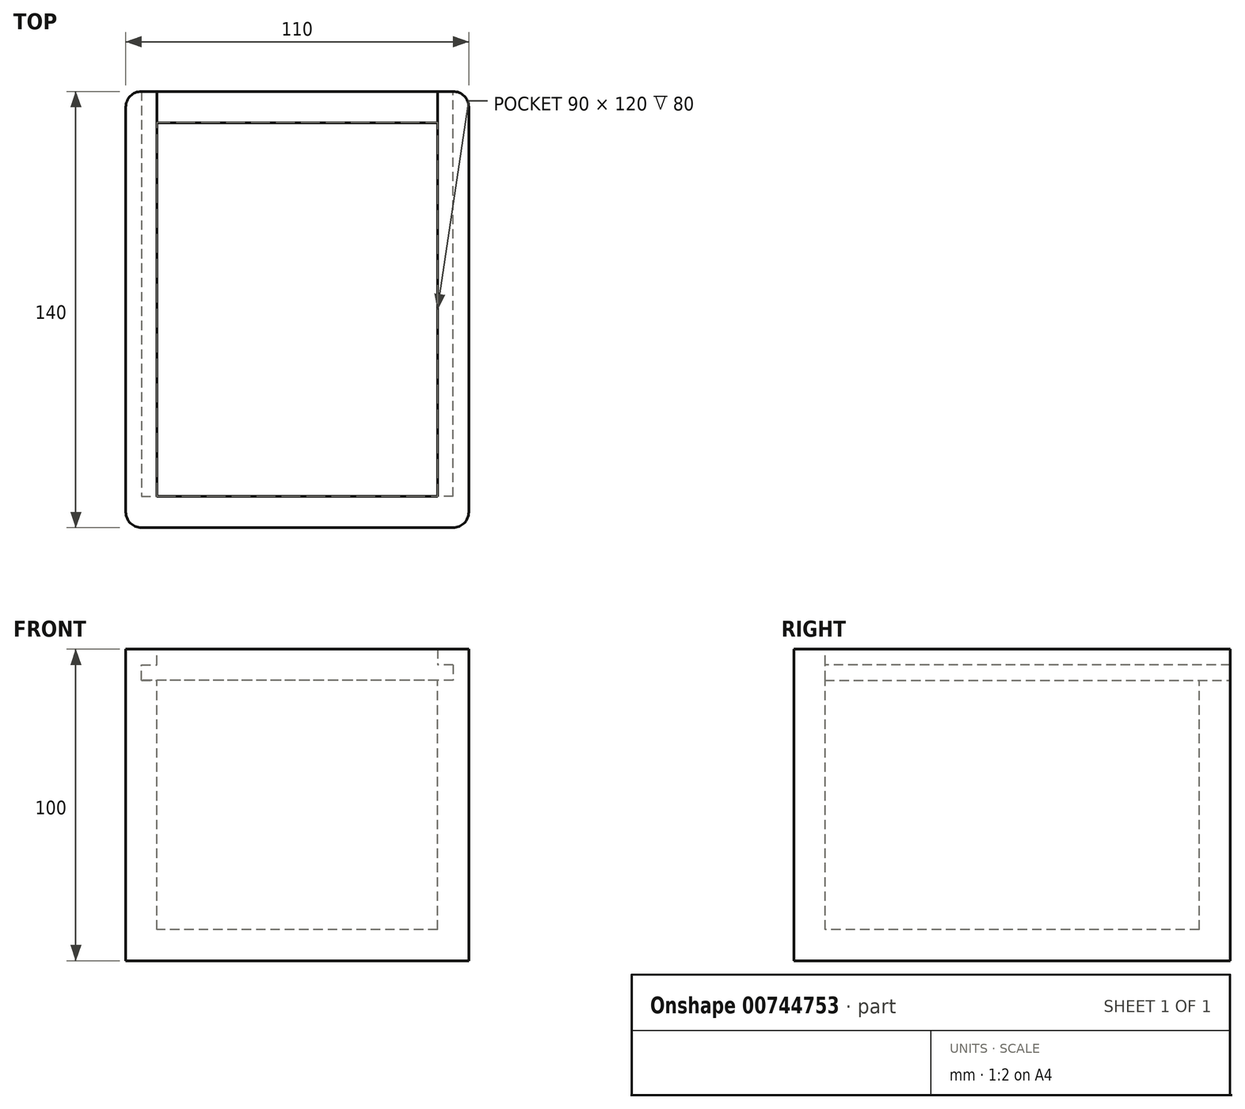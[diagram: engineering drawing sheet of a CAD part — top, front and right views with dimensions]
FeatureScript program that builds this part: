
annotation { "Feature Type Name" : "Feature", "Feature Type Description" : "" }
export const myFeature = defineFeature(function(context is Context, id is Id, definition is map)
    precondition{}
    {
        {
            var Q0;
            Q0=qCreatedBy(makeId("Top.planeOp"),FACE);
            var sketch = newSketch(context, id + "F0", { "sketchPlane" : qUnion([Q0])});
            skLineSegment(sketch, "E0.bottom", {"start": v(50, -70) * mm, "end": v(-50, -70) * mm});
            skLineSegment(sketch, "E0.top", {"start": v(50, 70) * mm, "end": v(-50, 70) * mm});
            skLineSegment(sketch, "E0.left", {"start": v(55, -65) * mm, "end": v(55, 65) * mm});
            skLineSegment(sketch, "E0.right", {"start": v(-55, -65) * mm, "end": v(-55, 65) * mm});
            skPoint(sketch, "E0.middle", {"position": v(0, 0) * mm});
            skPoint(sketch, "E1.visualSharp", {"position": v(-55, 70) * mm});
            skArc(sketch, "E1.filletArc", {"start": v(-50, 70) * mm, "mid": v(-53.54, 68.54) * mm, "end": v(-55, 65) * mm});
            skPoint(sketch, "E2.visualSharp", {"position": v(-55, -70) * mm});
            skArc(sketch, "E2.filletArc", {"start": v(-55, -65) * mm, "mid": v(-53.54, -68.54) * mm, "end": v(-50, -70) * mm});
            skPoint(sketch, "E3.visualSharp", {"position": v(55, -70) * mm});
            skArc(sketch, "E3.filletArc", {"start": v(50, -70) * mm, "mid": v(53.54, -68.54) * mm, "end": v(55, -65) * mm});
            skPoint(sketch, "E4.visualSharp", {"position": v(55, 70) * mm});
            skArc(sketch, "E4.filletArc", {"start": v(55, 65) * mm, "mid": v(53.54, 68.54) * mm, "end": v(50, 70) * mm});
            skSolve(sketch);
        }
        {
            var Q0;
            Q0=makeQuery(id+"F0.imprint","IMPRINT",FACE,{"disambiguationData":[TD([[makeQuery(id+"F0.imprint","IMPRINT",EDGE,{"derivedFrom":sQuery(id+"F0.wireOp",EDGE,"E0.bottom")}),-1.0]])]});
            extrude(context, id + "F1", {"entities" : qUnion([Q0]), "depth" : 100 * mm, "offsetDistance" : 25 * mm});
        }
        {
            var Q0;
            Q0=makeQuery(id+"F1.opExtrude","CAP_FACE",FACE,{"disambiguationData":[OSD([sQuery(id+"F0.wireOp",EDGE,"E0.bottom"),sQuery(id+"F0.wireOp",EDGE,"E0.top"),sQuery(id+"F0.wireOp",EDGE,"E0.left"),sQuery(id+"F0.wireOp",EDGE,"E0.right")])],"isStart":false});
            var sketch = newSketch(context, id + "F2", { "sketchPlane" : qUnion([Q0])});
            skLineSegment(sketch, "E5.bottom", {"start": v(45, 60) * mm, "end": v(-45, 60) * mm});
            skLineSegment(sketch, "E5.top", {"start": v(45, -60) * mm, "end": v(-45, -60) * mm});
            skLineSegment(sketch, "E5.left", {"start": v(45, 60) * mm, "end": v(45, -60) * mm});
            skLineSegment(sketch, "E5.right", {"start": v(-45, 60) * mm, "end": v(-45, -60) * mm});
            skPoint(sketch, "E5.middle", {"position": v(0, 0) * mm});
            skSolve(sketch);
        }
        {
            var Q0;
            Q0=makeQuery(id+"F2.imprint","IMPRINT",FACE,{"disambiguationData":[TD([[makeQuery(id+"F2.imprint","IMPRINT",EDGE,{"derivedFrom":sQuery(id+"F2.wireOp",EDGE,"E5.bottom")}),1.0]])]});
            extrude(context, id + "F3", {"entities" : qUnion([Q0]), "operationType" : NewBodyOperationType.REMOVE, "oppositeDirection" : true, "depth" : 90 * mm, "offsetDistance" : 25 * mm});
        }
        {
            var Q0;
            Q0=makeQuery(id+"F3.boolean.opBoolean","COPY",FACE,{"derivedFrom":makeQuery(id+"F3.opExtrude","SWEPT_FACE",FACE,{"disambiguationData":[OSD([sQuery(id+"F2.wireOp",EDGE,"E5.right")])]})});
            var sketch = newSketch(context, id + "F4", { "sketchPlane" : qUnion([Q0])});
            skLineSegment(sketch, "E6.bottom", {"start": v(60, 95) * mm, "end": v(-60, 95) * mm});
            skLineSegment(sketch, "E6.top", {"start": v(60, 90) * mm, "end": v(-60, 90) * mm});
            skLineSegment(sketch, "E6.left", {"start": v(60, 95) * mm, "end": v(60, 90) * mm});
            skLineSegment(sketch, "E6.right", {"start": v(-60, 95) * mm, "end": v(-60, 90) * mm});
            skPoint(sketch, "E6.middle", {"position": v(0, 92.5) * mm});
            skSolve(sketch);
        }
        {
            var Q0;
            Q0 = qSketchRegion(id + "F4", true);
            extrude(context, id + "F5", {"entities" : qUnion([Q0]), "operationType" : NewBodyOperationType.REMOVE, "oppositeDirection" : true, "depth" : 5 * mm, "offsetDistance" : 25 * mm});
        }
        {
            var Q0;
            Q0=makeQuery(id+"F3.boolean.opBoolean","COPY",FACE,{"derivedFrom":makeQuery(id+"F3.opExtrude","SWEPT_FACE",FACE,{"disambiguationData":[OSD([sQuery(id+"F2.wireOp",EDGE,"E5.left")])]})});
            var sketch = newSketch(context, id + "F6", { "sketchPlane" : qUnion([Q0])});
            skLineSegment(sketch, "E7.bottom", {"start": v(60, 95) * mm, "end": v(-60, 95) * mm});
            skLineSegment(sketch, "E7.top", {"start": v(60, 90) * mm, "end": v(-60, 90) * mm});
            skLineSegment(sketch, "E7.left", {"start": v(60, 95) * mm, "end": v(60, 90) * mm});
            skLineSegment(sketch, "E7.right", {"start": v(-60, 95) * mm, "end": v(-60, 90) * mm});
            skPoint(sketch, "E7.middle", {"position": v(0, 92.5) * mm});
            skSolve(sketch);
        }
        {
            var Q0;
            Q0 = qSketchRegion(id + "F6", true);
            extrude(context, id + "F7", {"entities" : qUnion([Q0]), "operationType" : NewBodyOperationType.REMOVE, "oppositeDirection" : true, "depth" : 5 * mm, "offsetDistance" : 25 * mm});
        }
        {
            var Q0;
            Q0=makeQuery(id+"F7.boolean.opBoolean","MERGE",FACE,{"derivedFrom":[makeQuery(id+"F5.boolean.opBoolean","MERGE",FACE,{"derivedFrom":[makeQuery(id+"F3.boolean.opBoolean","COPY",FACE,{"derivedFrom":makeQuery(id+"F3.opExtrude","SWEPT_FACE",FACE,{"disambiguationData":[OSD([sQuery(id+"F2.wireOp",EDGE,"E5.bottom")])]})}),makeQuery(id+"F5.opExtrude","SWEPT_FACE",FACE,{"disambiguationData":[OSD([sQuery(id+"F4.wireOp",EDGE,"E6.left")])]})]}),makeQuery(id+"F7.opExtrude","SWEPT_FACE",FACE,{"disambiguationData":[OSD([sQuery(id+"F6.wireOp",EDGE,"E7.right")])]})]});
            var sketch = newSketch(context, id + "F8", { "sketchPlane" : qUnion([Q0])});
            skLineSegment(sketch, "E8.bottom", {"start": v(45, 100) * mm, "end": v(-45, 100) * mm});
            skLineSegment(sketch, "E8.top", {"start": v(45, 90) * mm, "end": v(-45, 90) * mm});
            skLineSegment(sketch, "E8.left", {"start": v(45, 100) * mm, "end": v(45, 90) * mm});
            skLineSegment(sketch, "E8.right", {"start": v(-45, 100) * mm, "end": v(-45, 90) * mm});
            skPoint(sketch, "E8.middle", {"position": v(0, 95) * mm});
            skSolve(sketch);
        }
        {
            var Q0;
            Q0 = qSketchRegion(id + "F8", true);
            extrude(context, id + "F9", {"entities" : qUnion([Q0]), "operationType" : NewBodyOperationType.REMOVE, "oppositeDirection" : true, "depth" : 10 * mm, "offsetDistance" : 25 * mm});
        }
        {
            var Q0;
            Q0=makeQuery(id+"F9.boolean.opBoolean","MERGE",FACE,{"derivedFrom":[makeQuery(id+"F7.boolean.opBoolean","SPLIT",FACE,{"disambiguationData":[TD([makeQuery(id+"F7.opExtrude","SWEPT_FACE",FACE,{"disambiguationData":[OSD([sQuery(id+"F6.wireOp",EDGE,"E7.bottom")])]})])],"derivedFrom":makeQuery(id+"F3.boolean.opBoolean","COPY",FACE,{"derivedFrom":makeQuery(id+"F3.opExtrude","SWEPT_FACE",FACE,{"disambiguationData":[OSD([sQuery(id+"F2.wireOp",EDGE,"E5.left")])]})})}),makeQuery(id+"F9.opExtrude","SWEPT_FACE",FACE,{"disambiguationData":[OSD([sQuery(id+"F8.wireOp",EDGE,"E8.left")])]})]});
            var sketch = newSketch(context, id + "F10", { "sketchPlane" : qUnion([Q0])});
            skLineSegment(sketch, "E9.bottom", {"start": v(-60, 95) * mm, "end": v(-70, 95) * mm});
            skLineSegment(sketch, "E9.top", {"start": v(-60, 90) * mm, "end": v(-70, 90) * mm});
            skLineSegment(sketch, "E9.left", {"start": v(-60, 95) * mm, "end": v(-60, 90) * mm});
            skLineSegment(sketch, "E9.right", {"start": v(-70, 95) * mm, "end": v(-70, 90) * mm});
            skSolve(sketch);
        }
        {
            var Q0;
            Q0=makeQuery(id+"F10.imprint","IMPRINT",FACE,{"disambiguationData":[TD([[makeQuery(id+"F10.imprint","IMPRINT",EDGE,{"derivedFrom":sQuery(id+"F10.wireOp",EDGE,"E9.bottom")}),1.0]])]});
            extrude(context, id + "F11", {"entities" : qUnion([Q0]), "operationType" : NewBodyOperationType.REMOVE, "oppositeDirection" : true, "depth" : 5 * mm, "offsetDistance" : 25 * mm});
        }
        {
            var Q0;
            Q0=makeQuery(id+"F9.boolean.opBoolean","MERGE",FACE,{"derivedFrom":[makeQuery(id+"F5.boolean.opBoolean","SPLIT",FACE,{"disambiguationData":[TD([makeQuery(id+"F5.opExtrude","SWEPT_FACE",FACE,{"disambiguationData":[OSD([sQuery(id+"F4.wireOp",EDGE,"E6.bottom")])]})])],"derivedFrom":makeQuery(id+"F3.boolean.opBoolean","COPY",FACE,{"derivedFrom":makeQuery(id+"F3.opExtrude","SWEPT_FACE",FACE,{"disambiguationData":[OSD([sQuery(id+"F2.wireOp",EDGE,"E5.right")])]})})}),makeQuery(id+"F9.opExtrude","SWEPT_FACE",FACE,{"disambiguationData":[OSD([sQuery(id+"F8.wireOp",EDGE,"E8.right")])]})]});
            var sketch = newSketch(context, id + "F12", { "sketchPlane" : qUnion([Q0])});
            skLineSegment(sketch, "E10.bottom", {"start": v(60, 95) * mm, "end": v(70, 95) * mm});
            skLineSegment(sketch, "E10.top", {"start": v(60, 90) * mm, "end": v(70, 90) * mm});
            skLineSegment(sketch, "E10.left", {"start": v(60, 95) * mm, "end": v(60, 90) * mm});
            skLineSegment(sketch, "E10.right", {"start": v(70, 95) * mm, "end": v(70, 90) * mm});
            skSolve(sketch);
        }
        {
            var Q0;
            Q0=makeQuery(id+"F12.imprint","IMPRINT",FACE,{"disambiguationData":[TD([[makeQuery(id+"F12.imprint","IMPRINT",EDGE,{"derivedFrom":sQuery(id+"F12.wireOp",EDGE,"E10.bottom")}),-1.0]])]});
            extrude(context, id + "F13", {"entities" : qUnion([Q0]), "operationType" : NewBodyOperationType.REMOVE, "oppositeDirection" : true, "depth" : 5 * mm, "offsetDistance" : 25 * mm});
        }
    });
